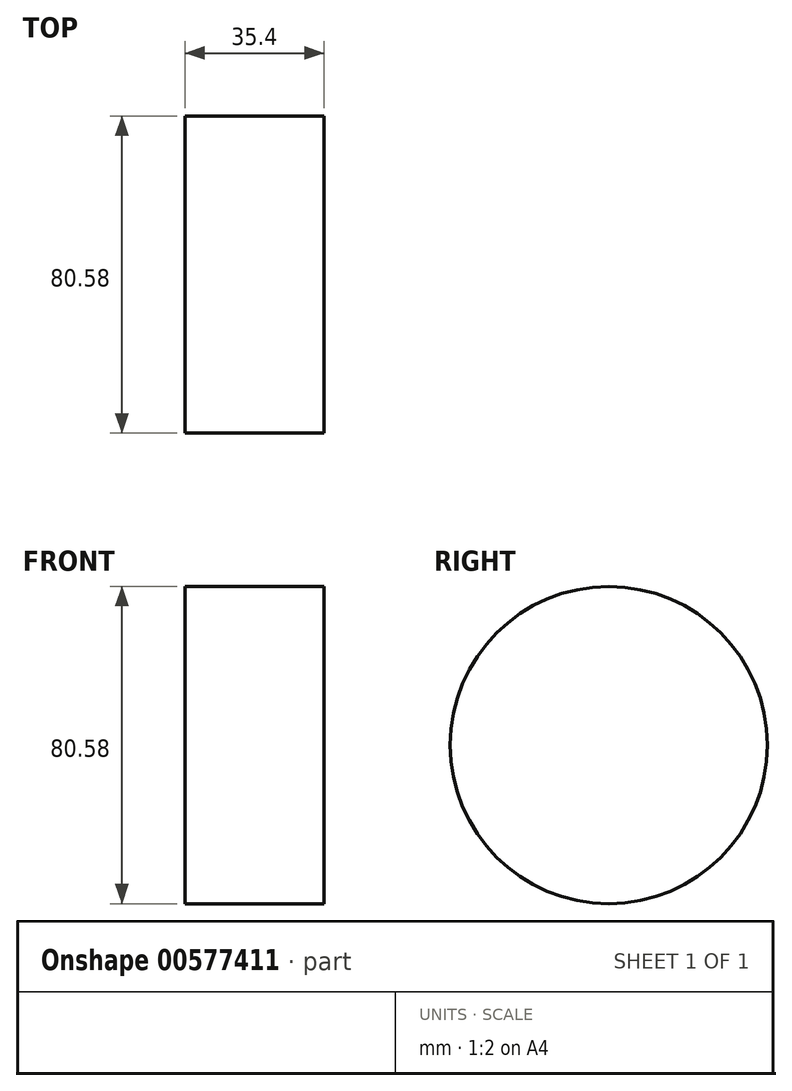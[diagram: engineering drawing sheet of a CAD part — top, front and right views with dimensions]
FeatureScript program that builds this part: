
annotation { "Feature Type Name" : "Feature", "Feature Type Description" : "" }
export const myFeature = defineFeature(function(context is Context, id is Id, definition is map)
    precondition{}
    {
        {
            var Q0;
            Q0=qCreatedBy(makeId("Right.planeOp"),FACE);
            var sketch = newSketch(context, id + "F0", { "sketchPlane" : qUnion([Q0])});
            skCircle(sketch, "E0", {"center": v(0, 0) * mm, "radius": 40.29 * mm});
            skSolve(sketch);
        }
        {
            var Q0;
            Q0 = qSketchRegion(id + "F0", true);
            extrude(context, id + "F1", {"entities" : qUnion([Q0]), "depth" : 35.4 * mm, "offsetDistance" : 25 * mm});
        }
    });
